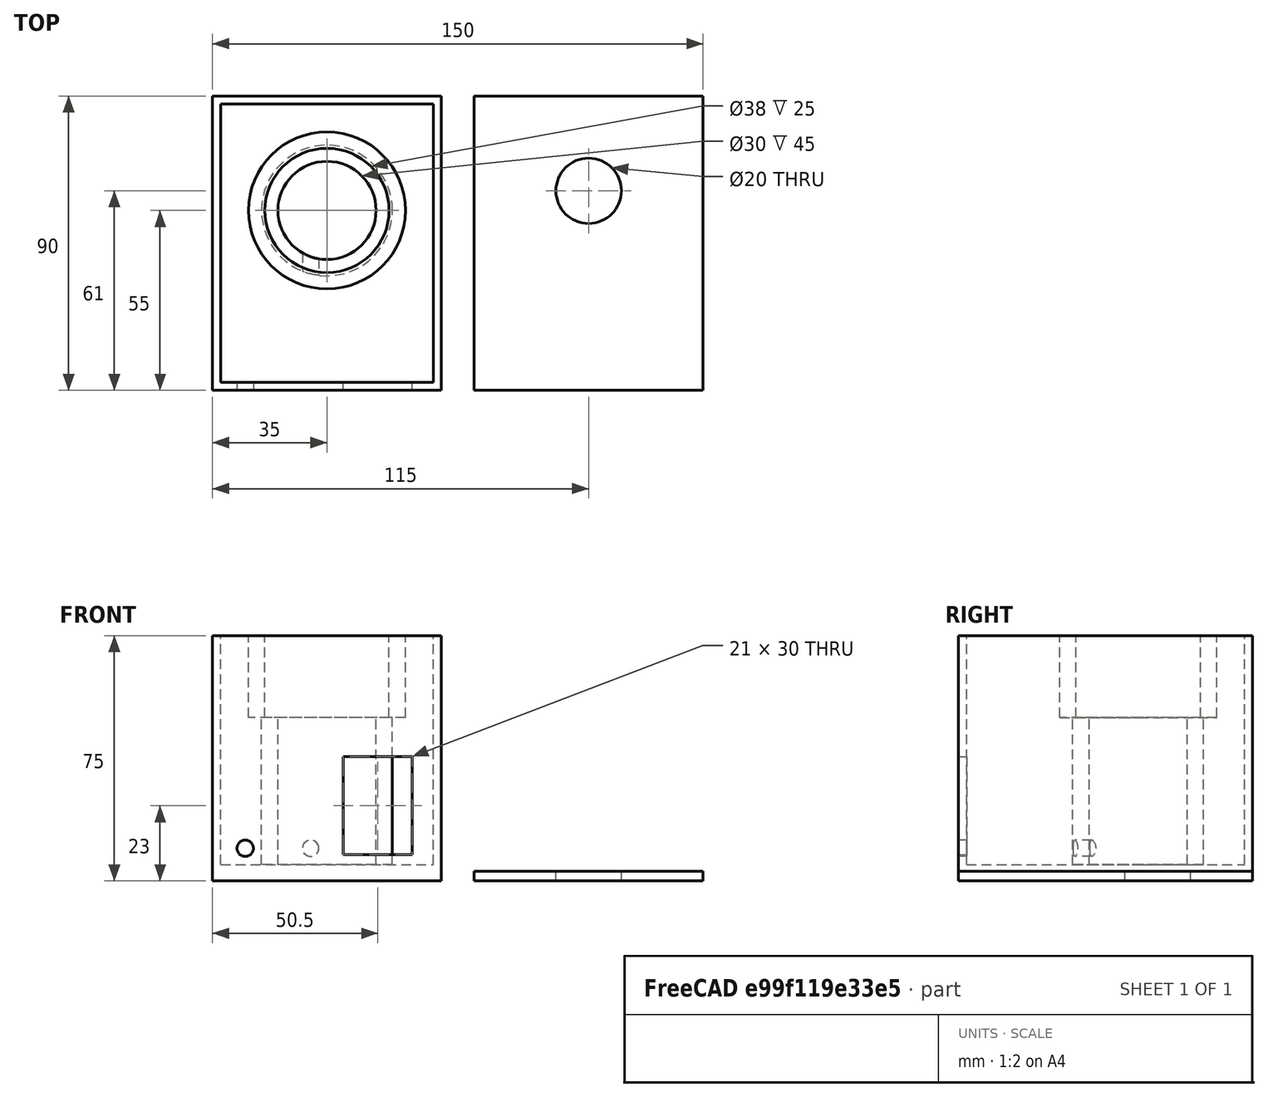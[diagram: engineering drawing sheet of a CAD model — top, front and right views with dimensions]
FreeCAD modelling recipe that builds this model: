
FCSTD DOCUMENT  (FreeCAD 0.17R13541 (Git))
Label: Motor_Holder
License: All rights reserved
LicenseURL: http://en.wikipedia.org/wiki/All_rights_reserved
objects: Part::Cylinder×7, Part::Cut×7, Part::Box×4, Part::MultiFuse×2
note: 20 computed .brp shape members not serialized (recipe doc carries the construction recipe); baked Part::Feature solids carry a one-line shape summary decoded from their .brp

FEATURE [Part::Cylinder] Cylinder
  Angle = 360
  AttacherType = Attacher::AttachEngine3D
  Height = 50
  Radius = 20
FEATURE [Part::Cylinder] Cylinder001
  Angle = 360
  AttacherType = Attacher::AttachEngine3D
  Height = 45
  Placement = pos=(0,0,5) rot=(0,0,1;0rad)
  Radius = 15
FEATURE [Part::Cut] Cut
  Base = -> Cylinder
  Tool = -> Cylinder001
FEATURE [Part::Cylinder] Cylinder002
  Angle = 360
  AttacherType = Attacher::AttachEngine3D
  Height = 25
  Radius = 24
FEATURE [Part::Cylinder] Cylinder003
  Angle = 360
  AttacherType = Attacher::AttachEngine3D
  Height = 25
  Radius = 19
FEATURE [Part::Cut] Cut001
  Base = -> Cylinder002
  Placement = pos=(0,0,50) rot=(0,0,1;0rad)
  Tool = -> Cylinder003
FEATURE [Part::Box] Box  label="Cube"
  AttacherType = Attacher::AttachEngine3D
  Height = 75
  Length = 70
  Placement = pos=(-35,-45,0) rot=(0,0,1;0rad)
  Width = 90
FEATURE [Part::Box] Box001  label="Cube001"
  AttacherType = Attacher::AttachEngine3D
  Height = 75
  Length = 65
  Placement = pos=(-32.5,-42.5,5) rot=(0,0,1;0rad)
  Width = 85
FEATURE [Part::Cut] Cut002
  Base = -> Box
  Placement = pos=(0,-10,0) rot=(0,0,1;0rad)
  Tool = -> Box001
FEATURE [Part::Box] Box002  label="Cube002"
  AttacherType = Attacher::AttachEngine3D
  Height = 30
  Length = 21
  Placement = pos=(5,-60,8) rot=(0,0,1;0rad)
  Width = 10
FEATURE [Part::Cut] Cut003
  Base = -> Cut002
  Tool = -> Box002
FEATURE [Part::Cylinder] Cylinder004
  Angle = 360
  AttacherType = Attacher::AttachEngine3D
  Height = 10
  Placement = pos=(-25,-45,10) rot=(1,0,0;1.5708rad)
  Radius = 2.5
FEATURE [Part::Cut] Cut004
  Base = -> Cut003
  Tool = -> Cylinder004
FEATURE [Part::Cylinder] Cylinder005
  Angle = 360
  AttacherType = Attacher::AttachEngine3D
  Height = 10
  Placement = pos=(-5,-10,10) rot=(1,0,0;1.5708rad)
  Radius = 2.5
FEATURE [Part::Cut] Cut005
  Base = -> Cut
  Tool = -> Cylinder005
FEATURE [Part::MultiFuse] Fusion
  Shapes = -> [Cut005,Cut001]
FEATURE [Part::MultiFuse] Fusion001
  Shapes = -> [Fusion,Cut004]
FEATURE [Part::Box] Box003  label="Cube003"
  AttacherType = Attacher::AttachEngine3D
  Height = 3
  Length = 70
  Placement = pos=(-35,-55,75) rot=(0,0,1;0rad)
  Width = 90
FEATURE [Part::Cylinder] Cylinder006
  Angle = 360
  AttacherType = Attacher::AttachEngine3D
  Height = 10
  Placement = pos=(0,6,70) rot=(0,0,1;0rad)
  Radius = 10
FEATURE [Part::Cut] Cut006
  Base = -> Box003
  Placement = pos=(80,0,-75) rot=(0,0,1;0rad)
  Tool = -> Cylinder006
